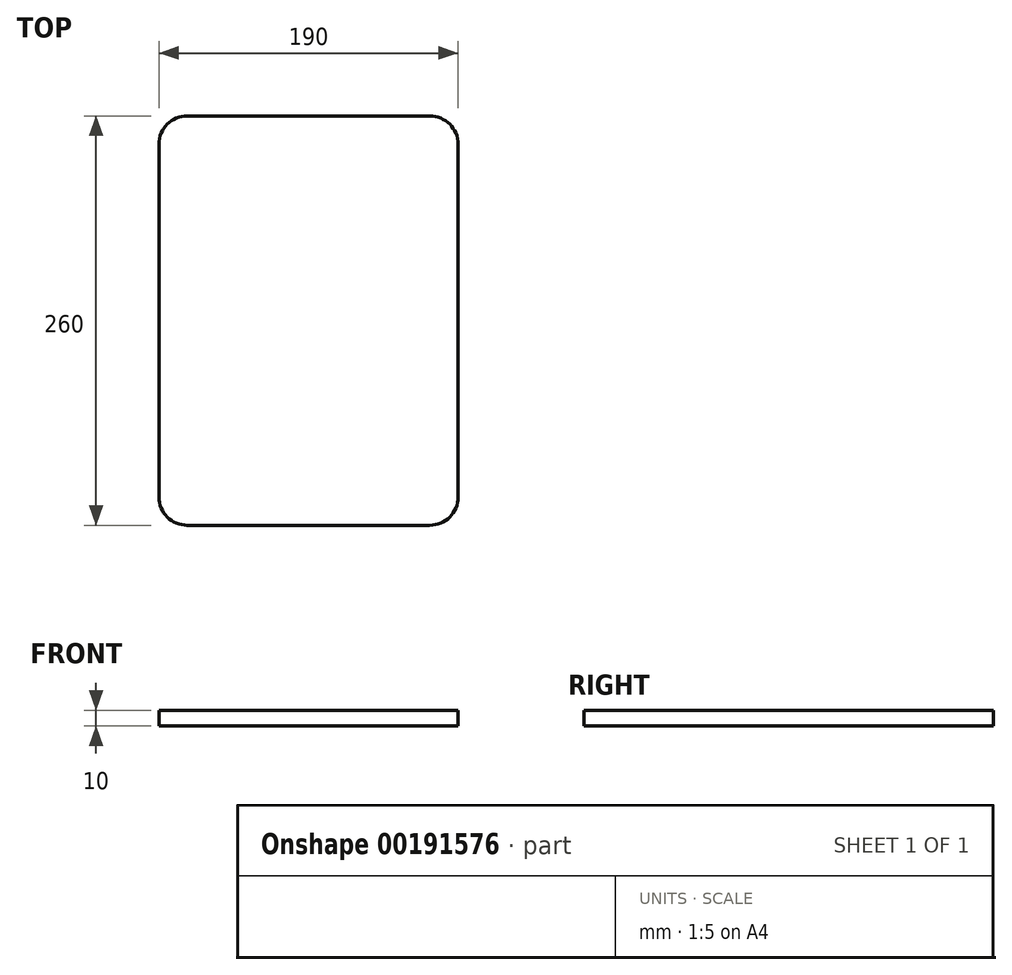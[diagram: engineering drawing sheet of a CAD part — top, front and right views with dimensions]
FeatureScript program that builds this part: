
annotation { "Feature Type Name" : "Feature", "Feature Type Description" : "" }
export const myFeature = defineFeature(function(context is Context, id is Id, definition is map)
    precondition{}
    {
        {
            var Q0;
            Q0=qCreatedBy(makeId("Top.planeOp"),FACE);
            var sketch = newSketch(context, id + "F0", { "sketchPlane" : qUnion([Q0])});
            skLineSegment(sketch, "E0.bottom", {"start": v(95, 130) * mm, "end": v(-95, 130) * mm});
            skLineSegment(sketch, "E0.top", {"start": v(95, -130) * mm, "end": v(-95, -130) * mm});
            skLineSegment(sketch, "E0.left", {"start": v(95, 130) * mm, "end": v(95, -130) * mm});
            skLineSegment(sketch, "E0.right", {"start": v(-95, 130) * mm, "end": v(-95, -130) * mm});
            skPoint(sketch, "E0.middle", {"position": v(0, 0) * mm});
            skSolve(sketch);
        }
        {
            var Q0;
            Q0 = qSketchRegion(id + "F0", true);
            extrude(context, id + "F1", {"entities" : qUnion([Q0]), "depth" : 10 * mm});
        }
        {
            var Q0;
            Q0=makeQuery(id+"F1.opExtrude","SWEPT_EDGE",EDGE,{"disambiguationData":[OSD([sQuery(id+"F0.wireOp",EDGE,"E0.top"),sQuery(id+"F0.wireOp",EDGE,"E0.left")])]});
            var Q1;
            Q1=makeQuery(id+"F1.opExtrude","SWEPT_EDGE",EDGE,{"disambiguationData":[OSD([sQuery(id+"F0.wireOp",EDGE,"E0.top"),sQuery(id+"F0.wireOp",EDGE,"E0.right")])]});
            var Q2;
            Q2=makeQuery(id+"F1.opExtrude","SWEPT_EDGE",EDGE,{"disambiguationData":[OSD([sQuery(id+"F0.wireOp",EDGE,"E0.bottom"),sQuery(id+"F0.wireOp",EDGE,"E0.left")])]});
            var Q3;
            Q3=makeQuery(id+"F1.opExtrude","SWEPT_EDGE",EDGE,{"disambiguationData":[OSD([sQuery(id+"F0.wireOp",EDGE,"E0.bottom"),sQuery(id+"F0.wireOp",EDGE,"E0.right")])]});
            fillet(context, id + "F2", {"entities" : qUnion([Q0, Q1, Q2, Q3]), "radius" : 18 * mm, "tangentPropagation" : true, "allowEdgeOverflow" : false});
        }
    });
